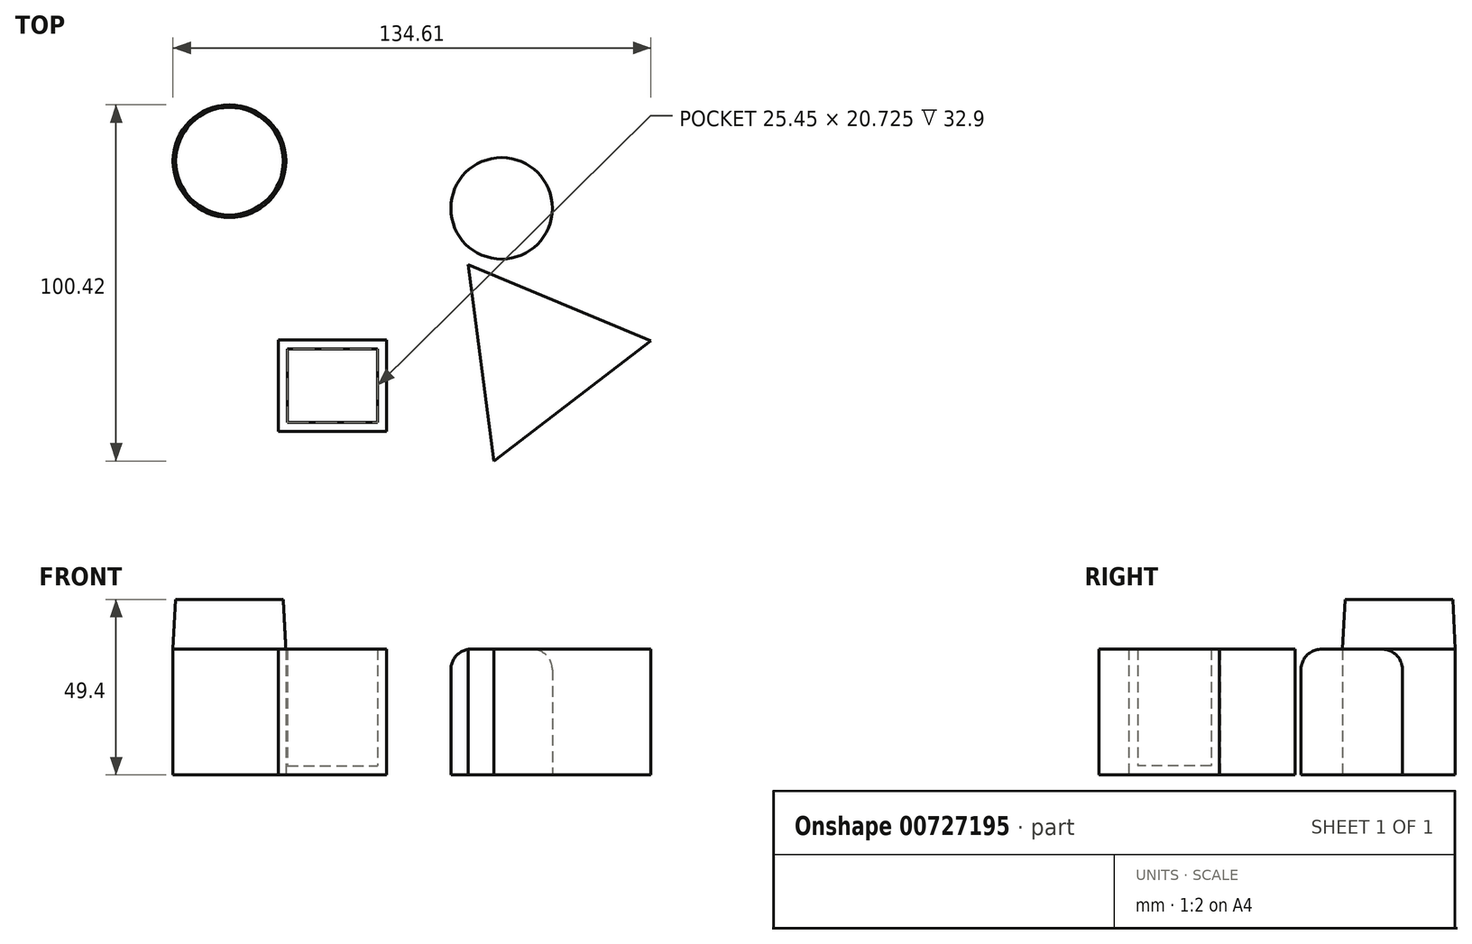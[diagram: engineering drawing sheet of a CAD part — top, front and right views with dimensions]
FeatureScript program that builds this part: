
annotation { "Feature Type Name" : "Feature", "Feature Type Description" : "" }
export const myFeature = defineFeature(function(context is Context, id is Id, definition is map)
    precondition{}
    {
        {
            var Q0;
            Q0=qCreatedBy(makeId("Top.planeOp"),FACE);
            var sketch = newSketch(context, id + "F0", { "sketchPlane" : qUnion([Q0])});
            skCircle(sketch, "E0", {"center": v(-59.41, 43.14) * mm, "radius": 15.9 * mm});
            skCircle(sketch, "E1", {"center": v(17.24, 29.84) * mm, "radius": 14.3 * mm});
            skLineSegment(sketch, "E2.bottom", {"start": v(-45.59, -7.26) * mm, "end": v(-15.14, -7.26) * mm});
            skLineSegment(sketch, "E2.top", {"start": v(-45.59, -32.99) * mm, "end": v(-15.14, -32.99) * mm});
            skLineSegment(sketch, "E2.left", {"start": v(-45.59, -7.26) * mm, "end": v(-45.59, -32.99) * mm});
            skLineSegment(sketch, "E2.right", {"start": v(-15.14, -7.26) * mm, "end": v(-15.14, -32.99) * mm});
            skCircle(sketch, "E3.cCircle", {"center": v(27.39, -11.64) * mm, "radius": 16.1 * mm, "construction": true});
            skLineSegment(sketch, "E3.0", {"start": v(59.31, -7.44) * mm, "end": v(15.06, -41.39) * mm});
            skLineSegment(sketch, "E3.1", {"start": v(15.06, -41.39) * mm, "end": v(7.79, 13.91) * mm});
            skLineSegment(sketch, "E3.2", {"start": v(7.79, 13.91) * mm, "end": v(59.31, -7.44) * mm});
            skPoint(sketch, "E3.0.midPoint", {"position": v(37.19, -24.41) * mm});
            skSolve(sketch);
        }
        {
            var Q0;
            Q0 = qSketchRegion(id + "F0", true);
            extrude(context, id + "F1", {"entities" : qUnion([Q0]), "depth" : 35.4 * mm, "offsetDistance" : 25 * mm});
        }
        {
            var Q0;
            Q0=makeQuery(id+"F1.opExtrude","CAP_FACE",FACE,{"disambiguationData":[OSD([sQuery(id+"F0.wireOp",EDGE,"E0")])],"isStart":false});
            var sketch = newSketch(context, id + "F2", { "sketchPlane" : qUnion([Q0])});
            skSolve(sketch);
        }
        {
            var Q0;
            Q0=makeQuery(id+"F2.imprint","IMPRINT",FACE,{"disambiguationData":[TD([[makeQuery(id+"F2.imprint","IMPRINT",EDGE,{"derivedFrom":makeQuery(id+"F1.opExtrude","CAP_EDGE",EDGE,{"disambiguationData":[OSD([sQuery(id+"F0.wireOp",EDGE,"E0")])],"isStart":false})}),1.0]])]});
            extrude(context, id + "F3", {"entities" : qUnion([Q0]), "operationType" : NewBodyOperationType.ADD, "depth" : 14 * mm, "offsetDistance" : 25 * mm, "hasDraft" : true, "draftAngle" : 3 * degree, "draftPullDirection" : true});
        }
        {
            var Q0;
            Q0=makeQuery(id+"F1.opExtrude","CAP_FACE",FACE,{"disambiguationData":[OSD([sQuery(id+"F0.wireOp",EDGE,"E2.bottom"),sQuery(id+"F0.wireOp",EDGE,"E2.top"),sQuery(id+"F0.wireOp",EDGE,"E2.left"),sQuery(id+"F0.wireOp",EDGE,"E2.right")])],"isStart":false});
            shell(context, id + "F4", {"entities" : qUnion([Q0]), "thickness" : 2.5 * mm});
        }
        {
            var Q0;
            Q0=makeQuery(id+"F1.opExtrude","CAP_EDGE",EDGE,{"disambiguationData":[OSD([sQuery(id+"F0.wireOp",EDGE,"E1")])],"isStart":false});
            fillet(context, id + "F5", {"entities" : qUnion([Q0]), "radius" : 5.8 * mm, "tangentPropagation" : true, "allowEdgeOverflow" : false});
        }
    });
